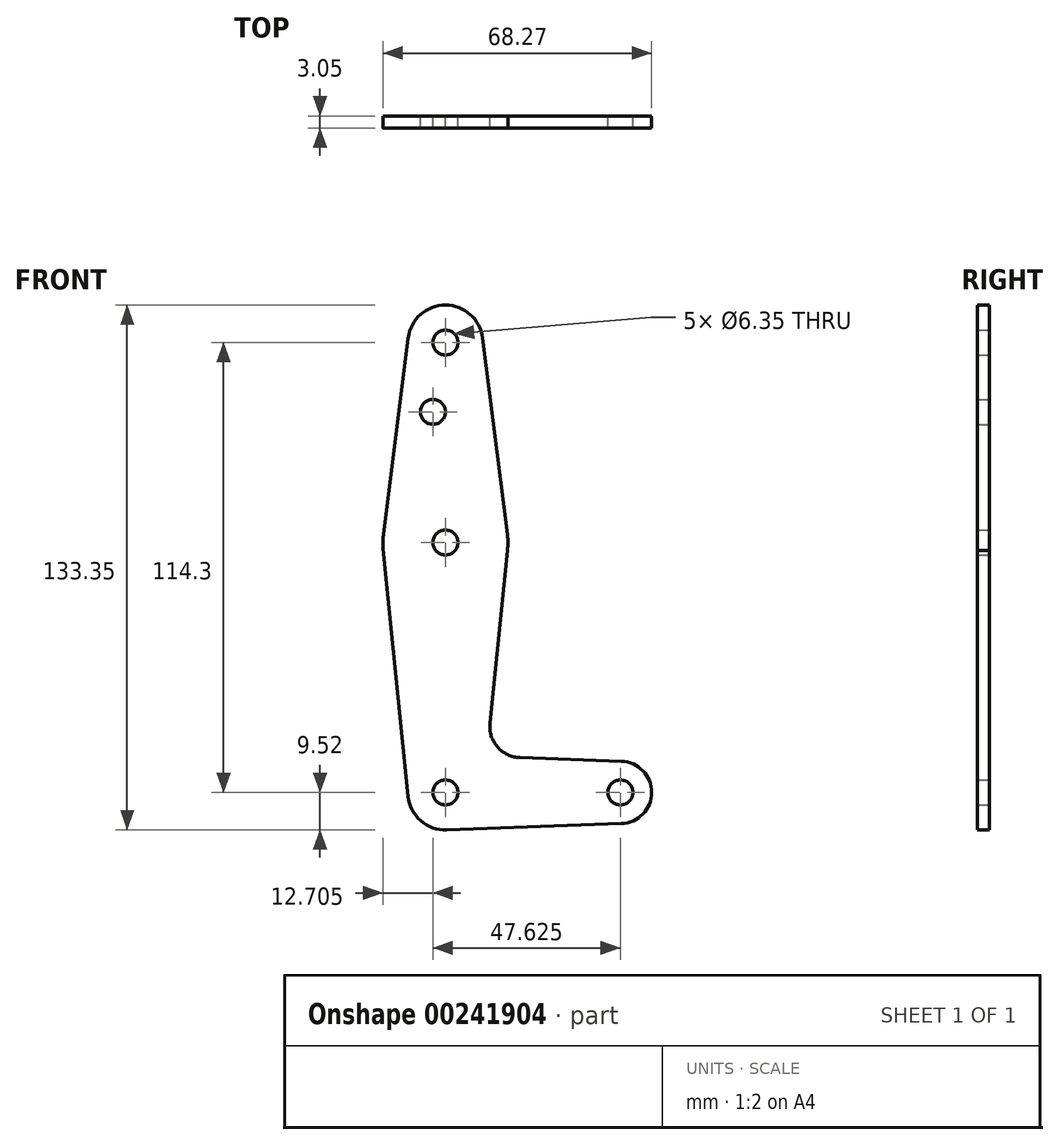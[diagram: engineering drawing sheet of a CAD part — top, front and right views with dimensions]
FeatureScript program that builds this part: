
annotation { "Feature Type Name" : "Feature", "Feature Type Description" : "" }
export const myFeature = defineFeature(function(context is Context, id is Id, definition is map)
    precondition{}
    {
        {
            var Q0;
            Q0=qCreatedBy(makeId("Front.planeOp"),FACE);
            var sketch = newSketch(context, id + "F0", { "sketchPlane" : qUnion([Q0])});
            skSolve(sketch);
        }
        {
            var Q0;
            Q0=qCreatedBy(makeId("Front.planeOp"),FACE);
            var sketch = newSketch(context, id + "F1", { "sketchPlane" : qUnion([Q0])});
            skCircle(sketch, "E0", {"center": v(0, 114.3) * mm, "radius": 9.52 * mm});
            skLineSegment(sketch, "E1", {"start": v(0, 0) * mm, "end": v(44.45, 0) * mm, "construction": true});
            skCircle(sketch, "E2", {"center": v(44.45, 0) * mm, "radius": 7.94 * mm});
            skCircle(sketch, "E3", {"center": v(0, 0) * mm, "radius": 9.52 * mm});
            skLineSegment(sketch, "E4", {"start": v(0, 114.3) * mm, "end": v(0, 0) * mm, "construction": true});
            skCircle(sketch, "E5", {"center": v(0, 63.5) * mm, "radius": 15.88 * mm});
            skLineSegment(sketch, "E6", {"start": v(9.45, 115.5) * mm, "end": v(15.75, 65.48) * mm});
            skLineSegment(sketch, "E7", {"start": v(-9.45, 115.5) * mm, "end": v(-15.75, 65.48) * mm});
            skLineSegment(sketch, "E8", {"start": v(0.34, -9.52) * mm, "end": v(44.73, -7.93) * mm});
            skLineSegment(sketch, "E9", {"start": v(-15.8, 61.91) * mm, "end": v(-9.48, -0.95) * mm});
            skLineSegment(sketch, "E10", {"start": v(15.75, 61.52) * mm, "end": v(11.3, 17.6) * mm});
            skLineSegment(sketch, "E11", {"start": v(18.93, 8.85) * mm, "end": v(44.73, 7.93) * mm});
            skCircle(sketch, "E12", {"center": v(0, 114.3) * mm, "radius": 3.18 * mm});
            skCircle(sketch, "E13", {"center": v(0, 63.5) * mm, "radius": 3.18 * mm});
            skCircle(sketch, "E14", {"center": v(0, 0) * mm, "radius": 3.18 * mm});
            skCircle(sketch, "E15", {"center": v(44.45, 0) * mm, "radius": 3.18 * mm});
            skCircle(sketch, "E16", {"center": v(-3.17, 96.7) * mm, "radius": 3.18 * mm});
            skArc(sketch, "E17.filletArc", {"start": v(11.3, 17.6) * mm, "mid": v(13.22, 11.57) * mm, "end": v(18.93, 8.85) * mm});
            skSolve(sketch);
        }
        {
            var Q0;
            Q0 = qSketchRegion(id + "F0", true);
            var Q1;
            {var subQ0=sQuery(id+"F1.wireOp",EDGE,"E8");Q1=makeQuery(id+"F1.imprint","IMPRINT",FACE,{"disambiguationData":[TD([[makeQuery(id+"F1.imprint","IMPRINT",EDGE,{"derivedFrom":subQ0}),1.0]])]});}
            var Q2;
            Q2=makeQuery(id+"F1.imprint","IMPRINT",FACE,{"disambiguationData":[TD([[makeQuery(id+"F1.imprint","IMPRINT",EDGE,{"derivedFrom":sQuery(id+"F1.wireOp",EDGE,"E13")}),-1.0]])]});
            var Q3;
            {var subQ0=sQuery(id+"F1.wireOp",EDGE,"E6");Q3=makeQuery(id+"F1.imprint","IMPRINT",FACE,{"disambiguationData":[TD([[makeQuery(id+"F1.imprint","IMPRINT",EDGE,{"derivedFrom":subQ0}),-1.0]])]});}
            var Q4;
            Q4=makeQuery(id+"F1.imprint","IMPRINT",FACE,{"disambiguationData":[TD([[makeQuery(id+"F1.imprint","IMPRINT",EDGE,{"derivedFrom":sQuery(id+"F1.wireOp",EDGE,"E12")}),-1.0]])]});
            var Q5;
            Q5=makeQuery(id+"F1.imprint","IMPRINT",FACE,{"disambiguationData":[TD([[makeQuery(id+"F1.imprint","IMPRINT",EDGE,{"derivedFrom":sQuery(id+"F1.wireOp",EDGE,"E14")}),-1.0]])]});
            var Q6;
            Q6=makeQuery(id+"F1.imprint","IMPRINT",FACE,{"disambiguationData":[TD([[makeQuery(id+"F1.imprint","IMPRINT",EDGE,{"derivedFrom":sQuery(id+"F1.wireOp",EDGE,"E15")}),-1.0]])]});
            extrude(context, id + "F2", {"entities" : qUnion([Q0, Q1, Q2, Q3, Q4, Q5, Q6]), "depth" : 3.05 * mm});
        }
    });
